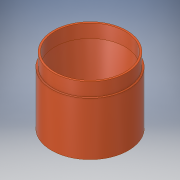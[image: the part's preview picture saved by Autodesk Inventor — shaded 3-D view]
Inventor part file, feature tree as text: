
AUTODESK INVENTOR PART (.ipt)
format: ipt  version: 2017 SP1 (Build 210196100, 196)  size: 168,960 bytes
history: native  units: in
note: dims shown in document units (in); Inventor stores cm internally (conversion verified against a paired STEP export)
features: revolve x1, sketch x1
ambient origin geometry x8: Origin, YZ Plane, XZ Plane, XY Plane, X Axis, Y Axis, Z Axis, Center Point
bodies: Solid1 (feature_tree)
feature tree (2):
  revolve  "Revolution1"  [1 undecoded]
  sketch  "Sketch1"  dims[d0=1.13in d1=3.75in d2=0.125in d3=0.1718in d5=1.0in d6=1.0in d7=90.0deg d8=0.5in d9=15.0deg d12=1.25in d13=0.25in d16=0.5in d17=0.5in d18=0.5in d19=2.5in d20=0.5in d22=0.375in d23=0.25in d25=0.234in d27=0.125in d28=0.25in d29=1.0in d30=4.25in d31=0.25in d33=0.8014in d34=15.0deg d35=0.125in d36=1.0in d37=90.0deg]
note: 1 required parameter value undecoded (feature->parameter linkage not recoverable at this tier; creation-order binding heuristic only, values carry confidence <= 0.55)
